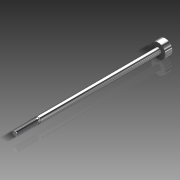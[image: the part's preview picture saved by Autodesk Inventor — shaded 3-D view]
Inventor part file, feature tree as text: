
AUTODESK INVENTOR PART (.ipt)
format: ipt  version: 2011 (Build 150239000, 239)  size: 86,528 bytes
history: native  units: in
note: dims shown in document units (in); Inventor stores cm internally (conversion verified against a paired STEP export)
features: other x1, imported_body x1, thread x1
ambient origin geometry x8: Origin, YZ Plane, XZ Plane, XY Plane, X Axis, Y Axis, Z Axis, Center Point
feature tree (3):
  parser-record x1  (decoder bookkeeping rows leaked as tree rows — omitted from the tree; the rows remain in map.json)
  imported_body  "Base1"
  thread  "Thread1"  [1 undecoded]
note: 1 required parameter value undecoded (feature->parameter linkage not recoverable at this tier; creation-order binding heuristic only, values carry confidence <= 0.55)
